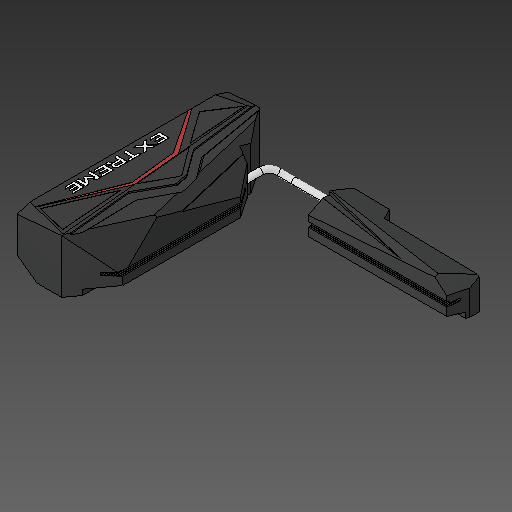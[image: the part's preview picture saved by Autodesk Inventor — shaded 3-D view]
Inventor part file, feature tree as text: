
AUTODESK INVENTOR PART (.ipt)
format: ipt  version: 2018.2 (Build 222227000, 227)  size: 377,856 bytes
history: native  units: mm
features: other x1, sweep x1
ambient origin geometry x8: Origin, YZ Plane, XZ Plane, XY Plane, X Axis, Y Axis, Z Axis, Center Point
bodies: Body1 (feature_tree)
feature tree (2):
  other  "ソリッド1"
  sweep  "Sweep1"
